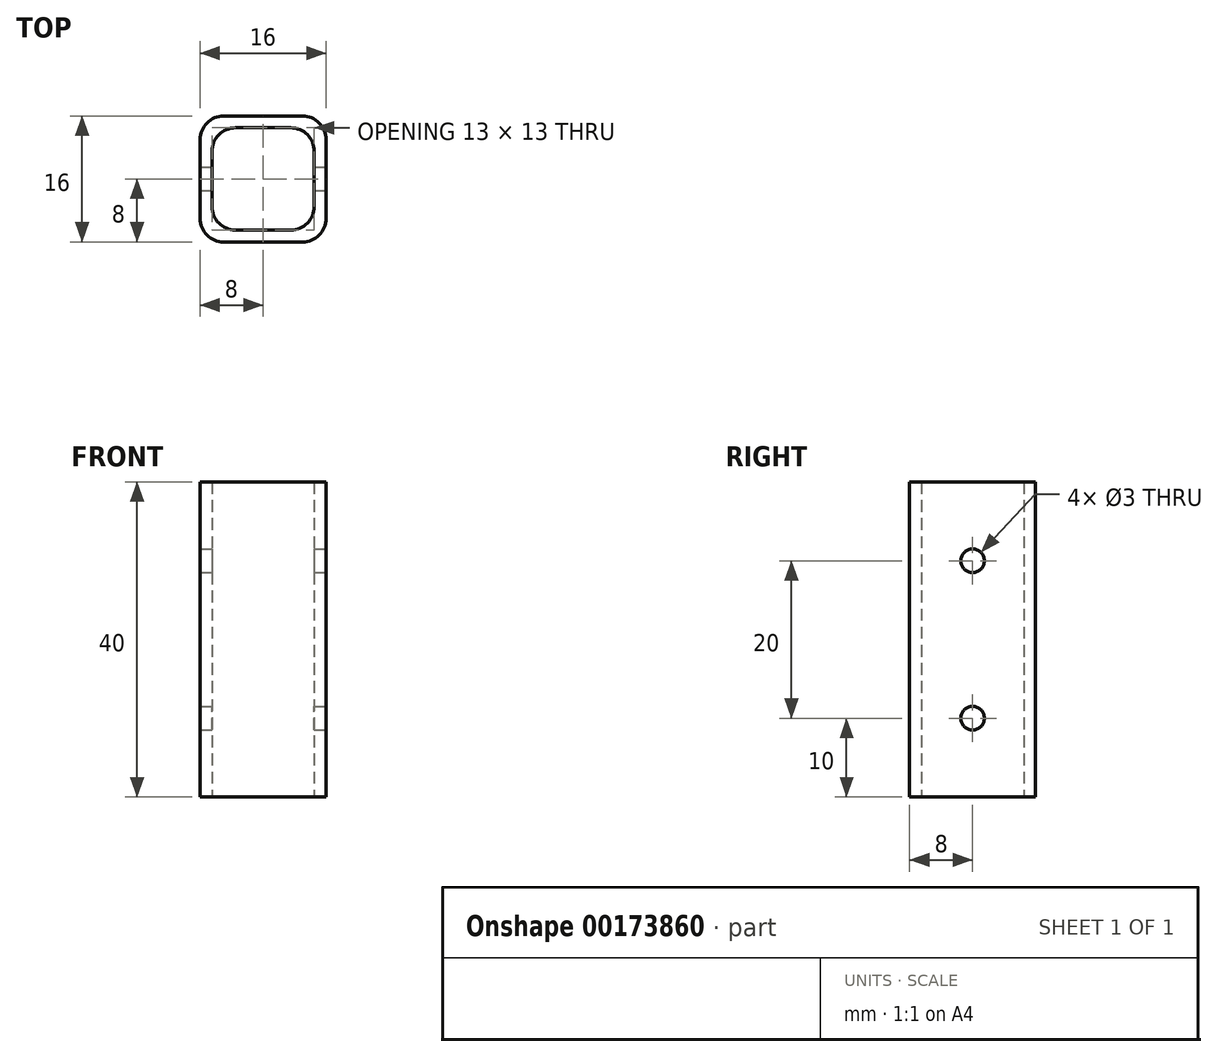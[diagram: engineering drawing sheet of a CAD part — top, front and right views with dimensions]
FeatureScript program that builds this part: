
annotation { "Feature Type Name" : "Feature", "Feature Type Description" : "" }
export const myFeature = defineFeature(function(context is Context, id is Id, definition is map)
    precondition{}
    {
        {
            var Q0;
            Q0=qCreatedBy(makeId("Top.planeOp"),FACE);
            var sketch = newSketch(context, id + "F0", { "sketchPlane" : qUnion([Q0])});
            skLineSegment(sketch, "E0.bottom", {"start": v(-3.5, -6.5) * mm, "end": v(3.5, -6.5) * mm});
            skLineSegment(sketch, "E0.top", {"start": v(-3.5, 6.5) * mm, "end": v(3.5, 6.5) * mm});
            skLineSegment(sketch, "E0.left", {"start": v(-6.5, -3.5) * mm, "end": v(-6.5, 3.5) * mm});
            skLineSegment(sketch, "E0.right", {"start": v(6.5, -3.5) * mm, "end": v(6.5, 3.5) * mm});
            skPoint(sketch, "E0.middle", {"position": v(0, 0) * mm});
            skPoint(sketch, "E1.visualSharp", {"position": v(-6.5, 6.5) * mm});
            skArc(sketch, "E1.filletArc", {"start": v(-3.5, 6.5) * mm, "mid": v(-5.62, 5.62) * mm, "end": v(-6.5, 3.5) * mm});
            skPoint(sketch, "E2.visualSharp", {"position": v(6.5, 6.5) * mm});
            skArc(sketch, "E2.filletArc", {"start": v(6.5, 3.5) * mm, "mid": v(5.62, 5.62) * mm, "end": v(3.5, 6.5) * mm});
            skPoint(sketch, "E3.visualSharp", {"position": v(6.5, -6.5) * mm});
            skArc(sketch, "E3.filletArc", {"start": v(3.5, -6.5) * mm, "mid": v(5.62, -5.62) * mm, "end": v(6.5, -3.5) * mm});
            skPoint(sketch, "E4.visualSharp", {"position": v(-6.5, -6.5) * mm});
            skArc(sketch, "E4.filletArc", {"start": v(-6.5, -3.5) * mm, "mid": v(-5.62, -5.62) * mm, "end": v(-3.5, -6.5) * mm});
            skLineSegment(sketch, "E5.bottom", {"start": v(-5, -8) * mm, "end": v(5, -8) * mm});
            skLineSegment(sketch, "E5.top", {"start": v(-5, 8) * mm, "end": v(5, 8) * mm});
            skLineSegment(sketch, "E5.left", {"start": v(-8, -5) * mm, "end": v(-8, 5) * mm});
            skLineSegment(sketch, "E5.right", {"start": v(8, -5) * mm, "end": v(8, 5) * mm});
            skPoint(sketch, "E6.visualSharp", {"position": v(-8, 8) * mm});
            skArc(sketch, "E6.filletArc", {"start": v(-5, 8) * mm, "mid": v(-7.12, 7.12) * mm, "end": v(-8, 5) * mm});
            skPoint(sketch, "E7.visualSharp", {"position": v(8, 8) * mm});
            skArc(sketch, "E7.filletArc", {"start": v(8, 5) * mm, "mid": v(7.12, 7.12) * mm, "end": v(5, 8) * mm});
            skPoint(sketch, "E8.visualSharp", {"position": v(8, -8) * mm});
            skArc(sketch, "E8.filletArc", {"start": v(5, -8) * mm, "mid": v(7.12, -7.12) * mm, "end": v(8, -5) * mm});
            skPoint(sketch, "E9.visualSharp", {"position": v(-8, -8) * mm});
            skArc(sketch, "E9.filletArc", {"start": v(-8, -5) * mm, "mid": v(-7.12, -7.12) * mm, "end": v(-5, -8) * mm});
            skSolve(sketch);
        }
        {
            var Q0;
            Q0=makeQuery(id+"F0.imprint","IMPRINT",FACE,{"disambiguationData":[TD([[makeQuery(id+"F0.imprint","IMPRINT",EDGE,{"derivedFrom":sQuery(id+"F0.wireOp",EDGE,"E0.bottom")}),-1.0]])]});
            extrude(context, id + "F1", {"entities" : qUnion([Q0]), "depth" : 20 * mm});
        }
        {
            var Q0;
            Q0=makeQuery(id+"F1.opExtrude","SWEPT_FACE",FACE,{"disambiguationData":[OSD([sQuery(id+"F0.wireOp",EDGE,"E5.right")])]});
            var sketch = newSketch(context, id + "F2", { "sketchPlane" : qUnion([Q0])});
            skLineSegment(sketch, "E10", {"start": v(0, 0) * mm, "end": v(0, 10) * mm});
            skPoint(sketch, "E10.endSnap0", {"position": v(0, 0) * mm});
            skCircle(sketch, "E11", {"center": v(0, 10) * mm, "radius": 1.5 * mm});
            skSolve(sketch);
        }
        {
            var Q0;
            Q0=makeQuery(id+"F2.imprint","IMPRINT",FACE,{"disambiguationData":[TD([[makeQuery(id+"F2.imprint","IMPRINT",EDGE,{"derivedFrom":sQuery(id+"F2.wireOp",EDGE,"E11")}),1.0]])]});
            extrude(context, id + "F3", {"entities" : qUnion([Q0]), "operationType" : NewBodyOperationType.REMOVE, "oppositeDirection" : true, "depth" : 25 * mm});
        }
        {
            var Q0;
            Q0=makeQuery(id+"F1.opExtrude","SWEPT_BODY",BODY,{"disambiguationData":[OSD([sQuery(id+"F0.wireOp",EDGE,"E0.bottom"),sQuery(id+"F0.wireOp",EDGE,"E0.top"),sQuery(id+"F0.wireOp",EDGE,"E0.left"),sQuery(id+"F0.wireOp",EDGE,"E0.right"),sQuery(id+"F0.wireOp",EDGE,"E1.filletArc"),sQuery(id+"F0.wireOp",EDGE,"E2.filletArc"),sQuery(id+"F0.wireOp",EDGE,"E3.filletArc"),sQuery(id+"F0.wireOp",EDGE,"E4.filletArc"),sQuery(id+"F0.wireOp",EDGE,"E5.bottom"),sQuery(id+"F0.wireOp",EDGE,"E5.top"),sQuery(id+"F0.wireOp",EDGE,"E5.left"),sQuery(id+"F0.wireOp",EDGE,"E5.right"),sQuery(id+"F0.wireOp",EDGE,"E6.filletArc"),sQuery(id+"F0.wireOp",EDGE,"E7.filletArc"),sQuery(id+"F0.wireOp",EDGE,"E8.filletArc"),sQuery(id+"F0.wireOp",EDGE,"E9.filletArc")])]});
            var Q1;
            Q1=qCreatedBy(makeId("Top.planeOp"),FACE);
            mirror(context, id + "F4", {"operationType" : NewBodyOperationType.ADD, "entities" : qUnion([Q0]), "mirrorPlane" : qUnion([Q1])});
        }
    });
